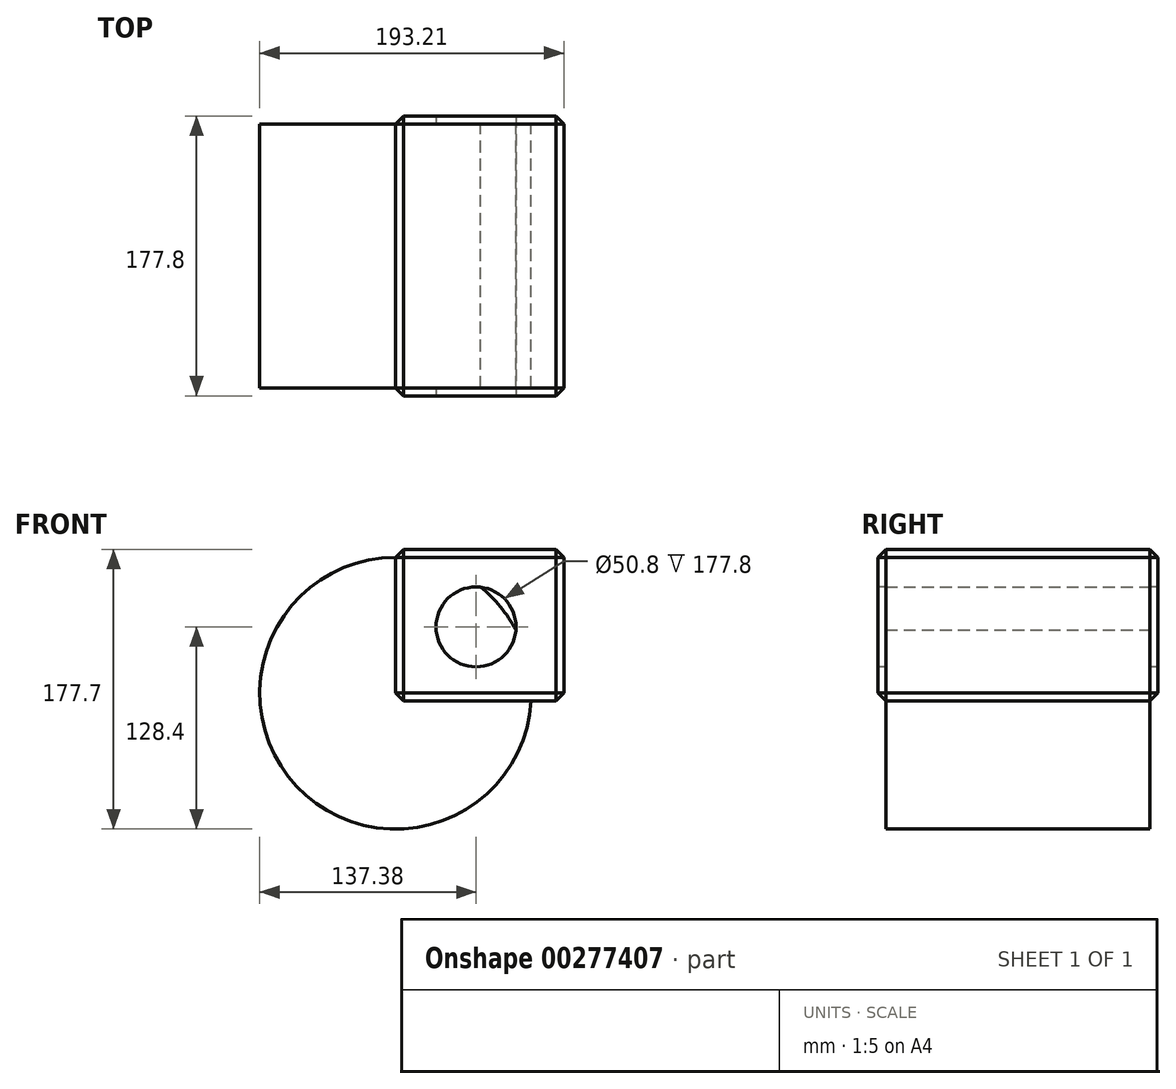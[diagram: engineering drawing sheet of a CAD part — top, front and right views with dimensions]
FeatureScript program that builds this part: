
annotation { "Feature Type Name" : "Feature", "Feature Type Description" : "" }
export const myFeature = defineFeature(function(context is Context, id is Id, definition is map)
    precondition{}
    {
        {
            var Q0;
            Q0=qCreatedBy(makeId("Front.planeOp"),FACE);
            var sketch = newSketch(context, id + "F3", { "sketchPlane" : qUnion([Q0])});
            skLineSegment(sketch, "E0.bottom", {"start": v(-51.07, 49.3) * mm, "end": v(55.83, 49.3) * mm});
            skLineSegment(sketch, "E0.top", {"start": v(-51.07, -47.17) * mm, "end": v(55.83, -47.17) * mm});
            skLineSegment(sketch, "E0.left", {"start": v(-51.07, 49.3) * mm, "end": v(-51.07, -47.17) * mm});
            skLineSegment(sketch, "E0.right", {"start": v(55.83, 49.3) * mm, "end": v(55.83, -47.17) * mm});
            skSolve(sketch);
        }
        {
            var Q0;
            Q0=makeQuery(id+"F3.imprint","IMPRINT",FACE,{"disambiguationData":[TD([[makeQuery(id+"F3.imprint","IMPRINT",EDGE,{"derivedFrom":sQuery(id+"F3.wireOp",EDGE,"E0.bottom")}),-1.0]])]});
            extrude(context, id + "F4", {"entities" : qUnion([Q0]), "depth" : 177.8 * mm});
        }
        {
            var Q0;
            Q0=makeQuery(id+"F4.opExtrude","SWEPT_EDGE",EDGE,{"disambiguationData":[OSD([sQuery(id+"F3.wireOp",EDGE,"E0.bottom"),sQuery(id+"F3.wireOp",EDGE,"E0.right")])]});
            var Q1;
            Q1=makeQuery(id+"F4.opExtrude","CAP_FACE",FACE,{"disambiguationData":[OSD([sQuery(id+"F3.wireOp",EDGE,"E0.bottom"),sQuery(id+"F3.wireOp",EDGE,"E0.top"),sQuery(id+"F3.wireOp",EDGE,"E0.left"),sQuery(id+"F3.wireOp",EDGE,"E0.right")])],"isStart":false});
            var Q2;
            Q2=makeQuery(id+"F4.opExtrude","CAP_FACE",FACE,{"disambiguationData":[OSD([sQuery(id+"F3.wireOp",EDGE,"E0.bottom"),sQuery(id+"F3.wireOp",EDGE,"E0.top"),sQuery(id+"F3.wireOp",EDGE,"E0.left"),sQuery(id+"F3.wireOp",EDGE,"E0.right")])],"isStart":true});
            var Q3;
            Q3=makeQuery(id+"F4.opExtrude","SWEPT_EDGE",EDGE,{"disambiguationData":[OSD([sQuery(id+"F3.wireOp",EDGE,"E0.top"),sQuery(id+"F3.wireOp",EDGE,"E0.left")])]});
            var Q4;
            Q4=makeQuery(id+"F4.opExtrude","SWEPT_EDGE",EDGE,{"disambiguationData":[OSD([sQuery(id+"F3.wireOp",EDGE,"E0.bottom"),sQuery(id+"F3.wireOp",EDGE,"E0.left")])]});
            var Q5;
            Q5=makeQuery(id+"F4.opExtrude","SWEPT_EDGE",EDGE,{"disambiguationData":[OSD([sQuery(id+"F3.wireOp",EDGE,"E0.top"),sQuery(id+"F3.wireOp",EDGE,"E0.right")])]});
            chamfer(context, id + "F5", {"entities" : qUnion([Q0, Q1, Q2, Q3, Q4, Q5]), "width" : 5.08 * mm, "tangentPropagation" : true});
        }
        {
            var Q0;
            Q0=makeQuery(id+"F4.opExtrude","CAP_FACE",FACE,{"disambiguationData":[OSD([sQuery(id+"F3.wireOp",EDGE,"E0.bottom"),sQuery(id+"F3.wireOp",EDGE,"E0.top"),sQuery(id+"F3.wireOp",EDGE,"E0.left"),sQuery(id+"F3.wireOp",EDGE,"E0.right")])],"isStart":false});
            var sketch = newSketch(context, id + "F0", { "sketchPlane" : qUnion([Q0])});
            skLineSegment(sketch, "E1", {"start": v(2.38, -42.1) * mm, "end": v(0, 0) * mm});
            skSolve(sketch);
        }
        {
            var Q0;
            Q0=sQuery(id+"F0.wireOp",VERTEX,"E1.end");
            var Q1;
            Q1=makeQuery(id+"F4.opExtrude","SWEPT_BODY",BODY,{"disambiguationData":[OSD([sQuery(id+"F3.wireOp",EDGE,"E0.bottom"),sQuery(id+"F3.wireOp",EDGE,"E0.top"),sQuery(id+"F3.wireOp",EDGE,"E0.left"),sQuery(id+"F3.wireOp",EDGE,"E0.right")])]});
            hole(context, id + "F1", {"style" : HoleStyle.SIMPLE, "endStyle" : HoleEndStyle.THROUGH, "holeDiameter" : 50.8 * mm, "tappedDepth" : 12.7 * mm, "tapClearance" : 3, "locations" : qUnion([Q0]), "scope" : qUnion([Q1])});
        }
        {
            var Q0;
            Q0=makeQuery(id+"F4.opExtrude","SWEPT_FACE",FACE,{"disambiguationData":[OSD([sQuery(id+"F3.wireOp",EDGE,"E0.left")])]});
            var Q1;
            {var subQ0=sQuery(id+"F3.wireOp",EDGE,"E0.left");Q1=makeQuery(id+"F5.opChamfer","BLEND_EDGE",EDGE,{"blendedFrom":[makeQuery(id+"F4.opExtrude","SWEPT_EDGE",EDGE,{"disambiguationData":[OSD([sQuery(id+"F3.wireOp",EDGE,"E0.top"),subQ0])]}),makeQuery(id+"F4.opExtrude","SWEPT_FACE",FACE,{"disambiguationData":[OSD([subQ0])]})],"blendedInto":[makeQuery(id+"F4.opExtrude","SWEPT_FACE",FACE,{"disambiguationData":[OSD([subQ0])]})]});}
            revolve(context, id + "F2", {"operationType" : NewBodyOperationType.ADD, "entities" : qUnion([Q0]), "axis" : qUnion([Q1]), "revolveType" : RevolveType.FULL});
        }
    });
